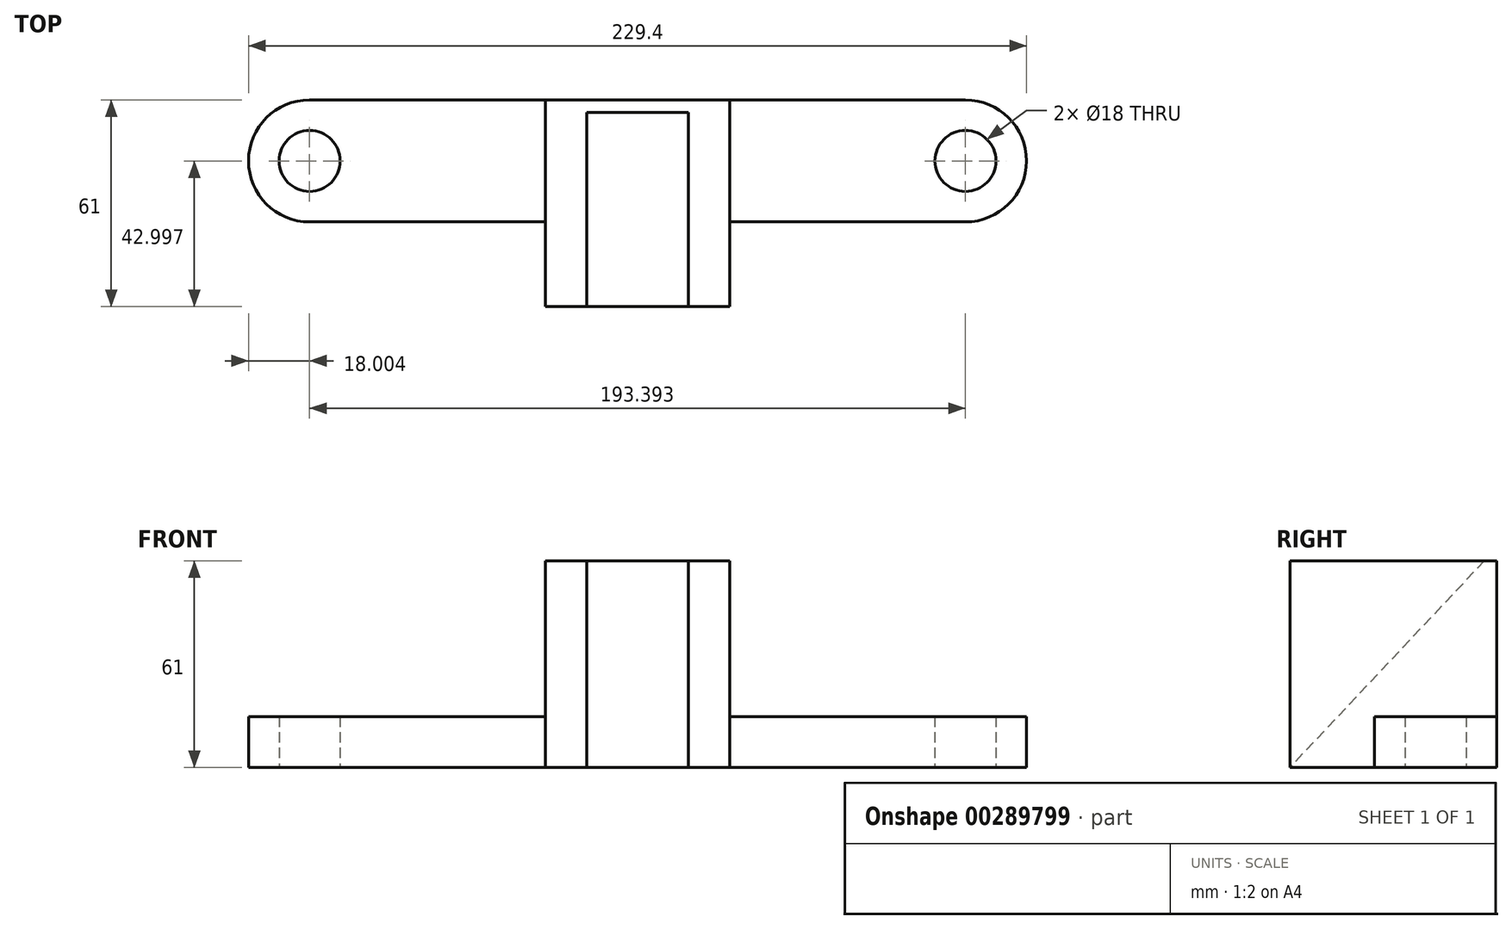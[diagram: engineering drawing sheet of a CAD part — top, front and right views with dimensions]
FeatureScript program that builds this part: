
annotation { "Feature Type Name" : "Feature", "Feature Type Description" : "" }
export const myFeature = defineFeature(function(context is Context, id is Id, definition is map)
    precondition{}
    {
        {
            var Q0;
            Q0=qCreatedBy(makeId("Top.planeOp"),FACE);
            var sketch = newSketch(context, id + "F0", { "sketchPlane" : qUnion([Q0])});
            skPoint(sketch, "E0.start.orphan", {"position": v(0, 14.93) * mm});
            skLineSegment(sketch, "E1", {"start": v(0, 48.48) * mm, "end": v(0, -47.41) * mm, "construction": true});
            skLineSegment(sketch, "E2", {"start": v(-96.7, 15.1) * mm, "end": v(0, 15.1) * mm});
            skPoint(sketch, "E3.end.orphan", {"position": v(-9.64, 20.57) * mm});
            skLineSegment(sketch, "E4", {"start": v(-27.17, 15.1) * mm, "end": v(-27.17, -45.9) * mm});
            skPoint(sketch, "E5.end.orphan", {"position": v(-27.17, -14.73) * mm});
            skPoint(sketch, "E6.orphan", {"position": v(0, 20.57) * mm});
            skLineSegment(sketch, "E7", {"start": v(-27.17, -45.9) * mm, "end": v(-15, -45.9) * mm});
            skLineSegment(sketch, "E8", {"start": v(0, 11.46) * mm, "end": v(-15, 11.46) * mm});
            skLineSegment(sketch, "E9", {"start": v(-15, 11.46) * mm, "end": v(-15, -45.9) * mm});
            skPoint(sketch, "E10.end.orphan", {"position": v(8.04, 11.46) * mm});
            skLineSegment(sketch, "E11", {"start": v(-27.17, -20.9) * mm, "end": v(-96.7, -20.9) * mm});
            skLineSegment(sketch, "E12", {"start": v(-96.7, -20.9) * mm, "end": v(-90.8, -20.9) * mm});
            skLineSegment(sketch, "E13", {"start": v(-90.8, -20.9) * mm, "end": v(-90.8, -19.9) * mm});
            skArc(sketch, "E14", {"start": v(-96.7, 15.1) * mm, "mid": v(-114.45, -5.88) * mm, "end": v(-90.8, -19.9) * mm});
            skCircle(sketch, "E15", {"center": v(-96.7, -2.9) * mm, "radius": 9 * mm});
            skLineSegment(sketch, "E16.MirrorCS", {"start": v(96.7, 15.1) * mm, "end": v(0, 15.1) * mm});
            skArc(sketch, "E17.MirrorCS", {"start": v(96.7, 15.1) * mm, "mid": v(114.45, -5.88) * mm, "end": v(90.8, -19.9) * mm});
            skCircle(sketch, "E18.MirrorC", {"center": v(96.7, -2.9) * mm, "radius": 9 * mm});
            skLineSegment(sketch, "E19.MirrorCS", {"start": v(27.17, -20.9) * mm, "end": v(96.7, -20.9) * mm});
            skLineSegment(sketch, "E20.MirrorCS", {"start": v(27.17, 15.1) * mm, "end": v(27.17, -45.9) * mm});
            skLineSegment(sketch, "E21.MirrorCS", {"start": v(27.17, -45.9) * mm, "end": v(15, -45.9) * mm});
            skLineSegment(sketch, "E22.MirrorCS", {"start": v(15, 11.46) * mm, "end": v(15, -45.9) * mm});
            skLineSegment(sketch, "E23.MirrorCS", {"start": v(0, 11.46) * mm, "end": v(15, 11.46) * mm});
            skSolve(sketch);
        }
        {
            var Q0;
            {var subQ10=sQuery(id+"F0.wireOp",EDGE,"E7");Q0=makeQuery(id+"F0.imprint","IMPRINT",FACE,{"disambiguationData":[TD([[makeQuery(id+"F0.imprint","IMPRINT",EDGE,{"derivedFrom":subQ10}),1.0]])]});}
            extrude(context, id + "F1", {"entities" : qUnion([Q0]), "depth" : 61 * mm});
        }
        {
            var Q0;
            Q0 = qSketchRegion(id + "F0", true);
            extrude(context, id + "F2", {"entities" : qUnion([Q0]), "operationType" : NewBodyOperationType.ADD, "depth" : 15 * mm});
        }
        {
            var Q0;
            Q0=makeQuery(id+"F1.opExtrude","SWEPT_FACE",FACE,{"disambiguationData":[OSD([sQuery(id+"F0.wireOp",EDGE,"E22.MirrorCS")])]});
            var sketch = newSketch(context, id + "F3", { "sketchPlane" : qUnion([Q0])});
            skLineSegment(sketch, "E24", {"start": v(-11.46, 61) * mm, "end": v(45.9, 0) * mm});
            skSolve(sketch);
        }
        {
            var Q0;
            Q0=makeQuery(id+"F3.imprint","IMPRINT",FACE,{"disambiguationData":[TD([[makeQuery(id+"F3.imprint","IMPRINT",EDGE,{"derivedFrom":sQuery(id+"F3.wireOp",EDGE,"E24")}),-1.0]])]});
            extrude(context, id + "F4", {"entities" : qUnion([Q0]), "operationType" : NewBodyOperationType.ADD, "depth" : 30 * mm});
        }
    });
